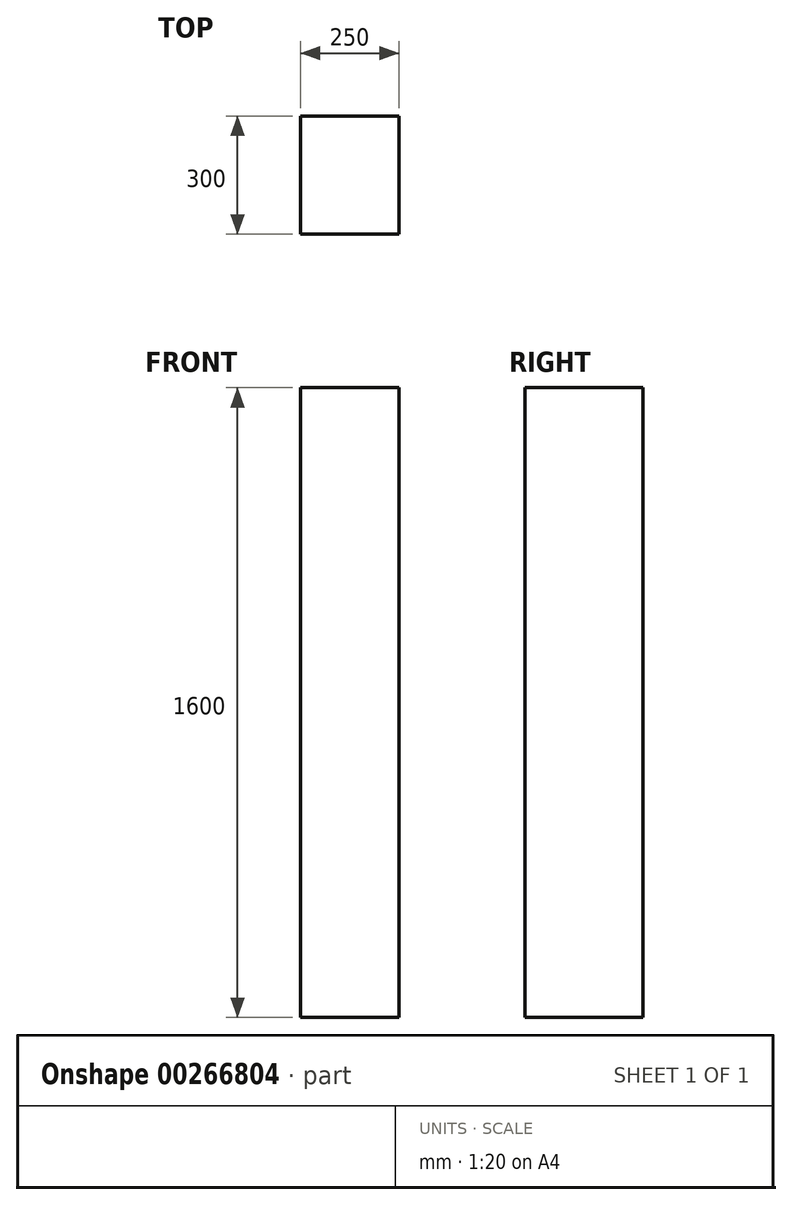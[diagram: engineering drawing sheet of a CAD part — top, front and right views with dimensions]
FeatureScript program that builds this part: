
annotation { "Feature Type Name" : "Feature", "Feature Type Description" : "" }
export const myFeature = defineFeature(function(context is Context, id is Id, definition is map)
    precondition{}
    {
        {
            var Q0;
            Q0=qCreatedBy(makeId("Front.planeOp"),FACE);
            var sketch = newSketch(context, id + "F0", { "sketchPlane" : qUnion([Q0])});
            skLineSegment(sketch, "E0.bottom", {"start": v(-515.2, 1246.5) * mm, "end": v(-265.2, 1246.5) * mm});
            skLineSegment(sketch, "E0.top", {"start": v(-515.2, -353.5) * mm, "end": v(-265.2, -353.5) * mm});
            skLineSegment(sketch, "E0.left", {"start": v(-515.2, 1246.5) * mm, "end": v(-515.2, -353.5) * mm});
            skLineSegment(sketch, "E0.right", {"start": v(-265.2, 1246.5) * mm, "end": v(-265.2, -353.5) * mm});
            skSolve(sketch);
        }
        {
            var Q0;
            Q0 = qSketchRegion(id + "F0", true);
            extrude(context, id + "F1", {"entities" : qUnion([Q0]), "depth" : 300 * mm});
        }
    });
